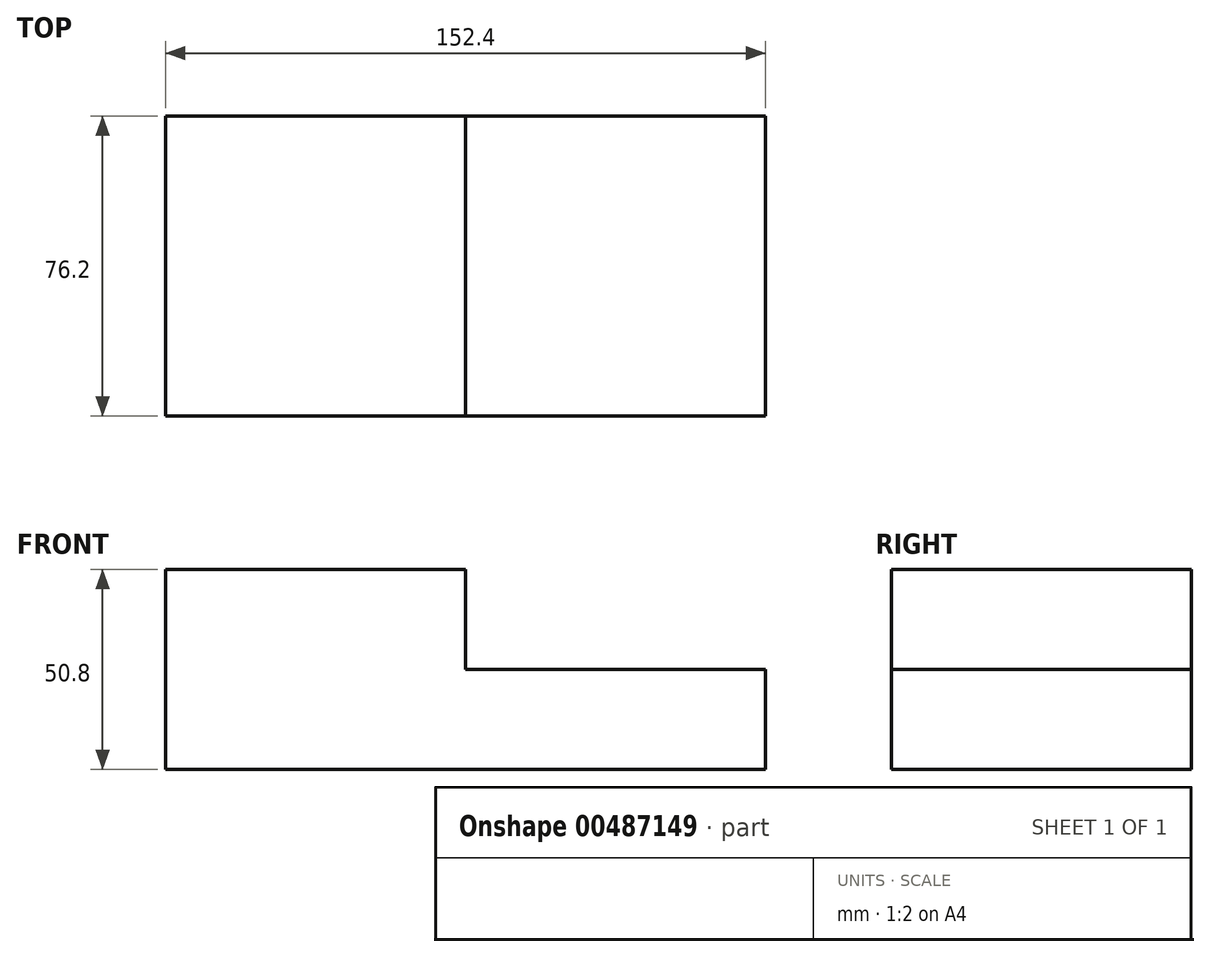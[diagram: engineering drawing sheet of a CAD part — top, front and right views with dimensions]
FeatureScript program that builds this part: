
annotation { "Feature Type Name" : "Feature", "Feature Type Description" : "" }
export const myFeature = defineFeature(function(context is Context, id is Id, definition is map)
    precondition{}
    {
        {
            var Q0;
            Q0=qCreatedBy(makeId("Front.planeOp"),FACE);
            var sketch = newSketch(context, id + "F0", { "sketchPlane" : qUnion([Q0])});
            skLineSegment(sketch, "E0", {"start": v(-69.57, -13.06) * mm, "end": v(82.83, -13.06) * mm});
            skLineSegment(sketch, "E1", {"start": v(82.83, -13.06) * mm, "end": v(82.83, 12.34) * mm});
            skLineSegment(sketch, "E2", {"start": v(82.83, 12.34) * mm, "end": v(6.63, 12.34) * mm});
            skLineSegment(sketch, "E3", {"start": v(6.63, 12.34) * mm, "end": v(6.63, 37.74) * mm});
            skLineSegment(sketch, "E4", {"start": v(6.63, 37.74) * mm, "end": v(-69.57, 37.74) * mm});
            skLineSegment(sketch, "E5", {"start": v(-69.57, 37.74) * mm, "end": v(-69.57, -13.06) * mm});
            skSolve(sketch);
        }
        {
            var Q0;
            Q0=makeQuery(id+"F0.imprint","IMPRINT",FACE,{"disambiguationData":[TD([[makeQuery(id+"F0.imprint","IMPRINT",EDGE,{"derivedFrom":sQuery(id+"F0.wireOp",EDGE,"E0")}),1.0]])]});
            extrude(context, id + "F1", {"entities" : qUnion([Q0]), "depth" : 76.2 * mm});
        }
    });
